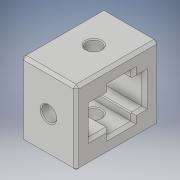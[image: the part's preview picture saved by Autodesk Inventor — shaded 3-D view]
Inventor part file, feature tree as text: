
AUTODESK INVENTOR PART (.ipt)
format: ipt  version: 2019 (Build 230136000, 136)  size: 212,992 bytes
history: native  units: mm
features: extrude x3, sketch x3, chamfer x2, projected_geometry x2, other x1
ambient origin geometry x8: Origin, YZ Plane, XZ Plane, XY Plane, X Axis, Y Axis, Z Axis, Center Point
bodies: Solide1 (feature_tree)
feature tree (11):
  extrude  "Extrusion1"  Depth=8.0mm
  extrude  "Extrusion2"  Depth=8.0mm
  extrude  "Extrusion3"  Depth=10.0mm
  chamfer  "Chanfrein1"  Distance=30.0mm
  chamfer  "Chanfrein2"  Distance=8.0mm
  sketch  "Esquisse1"
  sketch  "Esquisse2"
  sketch  "Esquisse4"
  projected_geometry  "Boucle projetée1"
  projected_geometry  "Boucle projetée2"
  other  "Projeter les arêtes coupées1"
